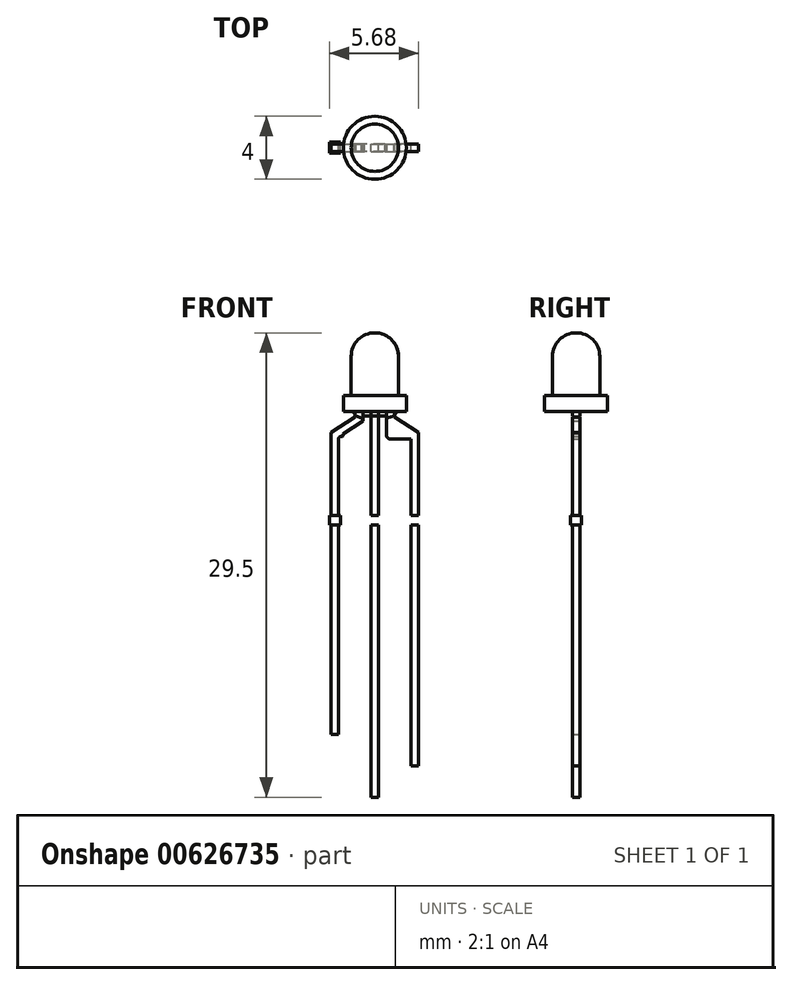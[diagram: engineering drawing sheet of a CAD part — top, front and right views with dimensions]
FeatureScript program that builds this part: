
annotation { "Feature Type Name" : "Feature", "Feature Type Description" : "" }
export const myFeature = defineFeature(function(context is Context, id is Id, definition is map)
    precondition{}
    {
        {
            var Q0;
            Q0=qCreatedBy(makeId("Front.planeOp"),FACE);
            var sketch = newSketch(context, id + "F0", { "sketchPlane" : qUnion([Q0])});
            skLineSegment(sketch, "E0", {"start": v(0, 0) * mm, "end": v(2, 0) * mm});
            skLineSegment(sketch, "E1", {"start": v(2, 0) * mm, "end": v(2, 1) * mm});
            skLineSegment(sketch, "E2", {"start": v(0, 0) * mm, "end": v(0, 1) * mm});
            skLineSegment(sketch, "E3", {"start": v(0, 1) * mm, "end": v(1.5, 1) * mm});
            skLineSegment(sketch, "E4", {"start": v(1.5, 1) * mm, "end": v(1.5, 3.5) * mm});
            skLineSegment(sketch, "E5", {"start": v(0, 5) * mm, "end": v(0, 5) * mm});
            skArc(sketch, "E6.filletArc", {"start": v(1.5, 3.5) * mm, "mid": v(1.06, 4.56) * mm, "end": v(0, 5) * mm});
            skLineSegment(sketch, "E7", {"start": v(1.5, 1) * mm, "end": v(2, 1) * mm});
            skLineSegment(sketch, "E8", {"start": v(0, 5) * mm, "end": v(0, 1) * mm});
            skSolve(sketch);
        }
        {
            var Q0;
            Q0=makeQuery(id+"F0.imprint","IMPRINT",FACE,{"disambiguationData":[TD([[makeQuery(id+"F0.imprint","IMPRINT",EDGE,{"derivedFrom":sQuery(id+"F0.wireOp",EDGE,"E3")}),1.0]])]});
            var Q1;
            Q1=makeQuery(id+"F0.imprint","IMPRINT",FACE,{"disambiguationData":[TD([[makeQuery(id+"F0.imprint","IMPRINT",EDGE,{"derivedFrom":sQuery(id+"F0.wireOp",EDGE,"E0")}),1.0]])]});
            var Q2;
            Q2=sQuery(id+"F0.wireOp",EDGE,"E8");
            revolve(context, id + "F1", {"entities" : qUnion([Q0, Q1]), "axis" : qUnion([Q2]), "revolveType" : RevolveType.FULL});
        }
        {
            var Q0;
            Q0=qCreatedBy(makeId("Front.planeOp"),FACE);
            var sketch = newSketch(context, id + "F2", { "sketchPlane" : qUnion([Q0])});
            skLineSegment(sketch, "E9", {"start": v(0, 0) * mm, "end": v(0.25, 0) * mm});
            skLineSegment(sketch, "E10", {"start": v(0.25, 0) * mm, "end": v(0.25, -24.5) * mm});
            skLineSegment(sketch, "E11", {"start": v(0.25, -24.5) * mm, "end": v(-0.25, -24.5) * mm});
            skLineSegment(sketch, "E12", {"start": v(-0.25, -24.5) * mm, "end": v(-0.25, 0) * mm});
            skLineSegment(sketch, "E13", {"start": v(-0.25, 0) * mm, "end": v(0, 0) * mm});
            skLineSegment(sketch, "E14", {"start": v(-2.29, -20.5) * mm, "end": v(-2.8, -20.5) * mm});
            skLineSegment(sketch, "E15", {"start": v(-2.8, -20.5) * mm, "end": v(-2.8, -1.6) * mm});
            skLineSegment(sketch, "E16", {"start": v(-2.29, -20.5) * mm, "end": v(-2.29, -1.7) * mm});
            skLineSegment(sketch, "E17", {"start": v(2.3, -22.5) * mm, "end": v(2.8, -22.5) * mm});
            skLineSegment(sketch, "E18", {"start": v(2.3, -22.5) * mm, "end": v(2.3, -1.74) * mm});
            skLineSegment(sketch, "E19", {"start": v(2.8, -22.5) * mm, "end": v(2.8, -1.6) * mm});
            skLineSegment(sketch, "E20", {"start": v(-0.25, 0) * mm, "end": v(-0.75, 0) * mm});
            skLineSegment(sketch, "E21", {"start": v(-0.75, 0) * mm, "end": v(-0.75, -0.6) * mm});
            skLineSegment(sketch, "E22", {"start": v(-0.75, 0) * mm, "end": v(-1.25, 0) * mm});
            skLineSegment(sketch, "E23", {"start": v(0.25, 0) * mm, "end": v(0.75, 0) * mm});
            skLineSegment(sketch, "E24", {"start": v(0.75, 0) * mm, "end": v(0.75, -0.6) * mm});
            skLineSegment(sketch, "E25", {"start": v(0.75, 0) * mm, "end": v(1.25, 0) * mm});
            skLineSegment(sketch, "E26", {"start": v(-2.8, -1.6) * mm, "end": v(-2.8, -1.34) * mm});
            skLineSegment(sketch, "E27", {"start": v(-2.8, -1.34) * mm, "end": v(-1.25, -0.34) * mm});
            skLineSegment(sketch, "E28", {"start": v(-1.25, -0.34) * mm, "end": v(-1.25, 0) * mm});
            skLineSegment(sketch, "E29", {"start": v(2.8, -1.6) * mm, "end": v(2.8, -1.34) * mm});
            skLineSegment(sketch, "E30", {"start": v(2.8, -1.34) * mm, "end": v(1.25, -0.34) * mm});
            skLineSegment(sketch, "E31", {"start": v(1.25, -0.34) * mm, "end": v(1.25, 0) * mm});
            skLineSegment(sketch, "E32", {"start": v(0.75, -0.6) * mm, "end": v(0.75, -1.54) * mm});
            skLineSegment(sketch, "E33", {"start": v(0.95, -1.74) * mm, "end": v(2.3, -1.74) * mm});
            skPoint(sketch, "E34.visualSharp", {"position": v(0.75, -1.74) * mm});
            skArc(sketch, "E34.filletArc", {"start": v(0.75, -1.54) * mm, "mid": v(0.8, -1.68) * mm, "end": v(0.95, -1.74) * mm});
            skLineSegment(sketch, "E35", {"start": v(-2.19, -1.6) * mm, "end": v(-2.1, -1.6) * mm});
            skLineSegment(sketch, "E36", {"start": v(-2, -1.5) * mm, "end": v(-2, -1.41) * mm});
            skLineSegment(sketch, "E37", {"start": v(-0.75, -0.6) * mm, "end": v(-2, -1.41) * mm});
            skPoint(sketch, "E38.visualSharp", {"position": v(-2.29, -1.6) * mm});
            skArc(sketch, "E38.filletArc", {"start": v(-2.19, -1.6) * mm, "mid": v(-2.26, -1.63) * mm, "end": v(-2.29, -1.7) * mm});
            skPoint(sketch, "E39.visualSharp", {"position": v(-2, -1.6) * mm});
            skArc(sketch, "E39.filletArc", {"start": v(-2.1, -1.6) * mm, "mid": v(-2.03, -1.57) * mm, "end": v(-2, -1.5) * mm});
            skLineSegment(sketch, "E40", {"start": v(0, -6.6) * mm, "end": v(4.77, -6.6) * mm});
            skLineSegment(sketch, "E41", {"start": v(0, -6.6) * mm, "end": v(-4.5, -6.6) * mm});
            skLineSegment(sketch, "E42", {"start": v(-2.8, -6.6) * mm, "end": v(-2.89, -6.6) * mm});
            skLineSegment(sketch, "E43", {"start": v(-2.89, -6.6) * mm, "end": v(-2.89, -7.2) * mm});
            skLineSegment(sketch, "E44", {"start": v(-2.89, -7.2) * mm, "end": v(-2.8, -7.2) * mm});
            skLineSegment(sketch, "E45", {"start": v(-2.29, -6.6) * mm, "end": v(-2.2, -6.6) * mm});
            skLineSegment(sketch, "E46", {"start": v(-2.2, -6.6) * mm, "end": v(-2.2, -7.2) * mm});
            skLineSegment(sketch, "E47", {"start": v(-2.2, -7.2) * mm, "end": v(-2.29, -7.2) * mm});
            skLineSegment(sketch, "E48.bottom", {"start": v(-0.25, -6.6) * mm, "end": v(-0.35, -6.6) * mm});
            skLineSegment(sketch, "E48.top", {"start": v(-0.25, -7.2) * mm, "end": v(-0.35, -7.2) * mm});
            skLineSegment(sketch, "E48.left", {"start": v(-0.25, -6.6) * mm, "end": v(-0.25, -7.2) * mm});
            skLineSegment(sketch, "E48.right", {"start": v(-0.35, -6.6) * mm, "end": v(-0.35, -7.2) * mm});
            skLineSegment(sketch, "E49.bottom", {"start": v(0.25, -6.6) * mm, "end": v(0.35, -6.6) * mm});
            skLineSegment(sketch, "E49.top", {"start": v(0.25, -7.2) * mm, "end": v(0.35, -7.2) * mm});
            skLineSegment(sketch, "E49.left", {"start": v(0.25, -6.6) * mm, "end": v(0.25, -7.2) * mm});
            skLineSegment(sketch, "E49.right", {"start": v(0.35, -6.6) * mm, "end": v(0.35, -7.2) * mm});
            skLineSegment(sketch, "E50.bottom", {"start": v(2.3, -6.6) * mm, "end": v(2.2, -6.6) * mm});
            skLineSegment(sketch, "E50.top", {"start": v(2.3, -7.2) * mm, "end": v(2.2, -7.2) * mm});
            skLineSegment(sketch, "E50.left", {"start": v(2.3, -6.6) * mm, "end": v(2.3, -7.2) * mm});
            skLineSegment(sketch, "E50.right", {"start": v(2.2, -6.6) * mm, "end": v(2.2, -7.2) * mm});
            skLineSegment(sketch, "E51.bottom", {"start": v(2.8, -6.6) * mm, "end": v(2.9, -6.6) * mm});
            skLineSegment(sketch, "E51.top", {"start": v(2.8, -7.2) * mm, "end": v(2.9, -7.2) * mm});
            skLineSegment(sketch, "E51.left", {"start": v(2.8, -6.6) * mm, "end": v(2.8, -7.2) * mm});
            skLineSegment(sketch, "E51.right", {"start": v(2.9, -6.6) * mm, "end": v(2.9, -7.2) * mm});
            skLineSegment(sketch, "E52.bottom", {"start": v(-2.89, -6.6) * mm, "end": v(-2.2, -6.6) * mm});
            skLineSegment(sketch, "E52.top", {"start": v(-2.89, -7.2) * mm, "end": v(-2.2, -7.2) * mm});
            skLineSegment(sketch, "E53.bottom", {"start": v(-0.35, -6.6) * mm, "end": v(0.35, -6.6) * mm});
            skLineSegment(sketch, "E53.top", {"start": v(-0.35, -7.2) * mm, "end": v(0.35, -7.2) * mm});
            skLineSegment(sketch, "E54.bottom", {"start": v(2.2, -6.6) * mm, "end": v(2.9, -6.6) * mm});
            skLineSegment(sketch, "E54.top", {"start": v(2.2, -7.2) * mm, "end": v(2.9, -7.2) * mm});
            skSolve(sketch);
        }
        {
            var Q0;
            Q0=makeQuery(id+"F2.imprint","IMPRINT",FACE,{"disambiguationData":[TD([[makeQuery(id+"F2.imprint","IMPRINT",EDGE,{"derivedFrom":sQuery(id+"F2.wireOp",EDGE,"E14")}),-1.0]])]});
            var Q1;
            Q1=makeQuery(id+"F2.imprint","IMPRINT",FACE,{"disambiguationData":[TD([[makeQuery(id+"F2.imprint","IMPRINT",EDGE,{"derivedFrom":sQuery(id+"F2.wireOp",EDGE,"E9")}),-1.0]])]});
            var Q2;
            Q2=makeQuery(id+"F2.imprint","IMPRINT",FACE,{"disambiguationData":[TD([[makeQuery(id+"F2.imprint","IMPRINT",EDGE,{"derivedFrom":sQuery(id+"F2.wireOp",EDGE,"E17")}),1.0]])]});
            var Q3;
            Q3=makeQuery(id+"F2.imprint","IMPRINT",FACE,{"disambiguationData":[TD([[makeQuery(id+"F2.imprint","IMPRINT",EDGE,{"derivedFrom":sQuery(id+"F2.wireOp",EDGE,"E24")}),1.0]])]});
            var Q4;
            Q4=makeQuery(id+"F2.imprint","IMPRINT",FACE,{"disambiguationData":[TD([[makeQuery(id+"F2.imprint","IMPRINT",EDGE,{"derivedFrom":sQuery(id+"F2.wireOp",EDGE,"E21")}),-1.0]])]});
            var Q5;
            {var subQ0=sQuery(id+"F2.wireOp",EDGE,"E11");Q5=makeQuery(id+"F2.imprint","IMPRINT",FACE,{"disambiguationData":[TD([[makeQuery(id+"F2.imprint","IMPRINT",EDGE,{"derivedFrom":subQ0}),-1.0]])]});}
            extrude(context, id + "F3", {"entities" : qUnion([Q0, Q1, Q2, Q3, Q4, Q5]), "endBound" : BoundingType.SYMMETRIC, "depth" : 0.5 * mm, "offsetDistance" : 25 * mm});
        }
        {
            var Q0;
            Q0=qCreatedBy(makeId("Front.planeOp"),FACE);
            var sketch = newSketch(context, id + "F4", { "sketchPlane" : qUnion([Q0])});
            skLineSegment(sketch, "E55", {"start": v(0, 0) * mm, "end": v(0, -0.3) * mm});
            skLineSegment(sketch, "E56", {"start": v(0, -0.3) * mm, "end": v(0.42, -0.3) * mm});
            skLineSegment(sketch, "E57", {"start": v(0, -0.3) * mm, "end": v(-0.42, -0.3) * mm});
            skLineSegment(sketch, "E58", {"start": v(0.42, -0.3) * mm, "end": v(0.65, -0.3) * mm});
            skLineSegment(sketch, "E59", {"start": v(0.65, -0.3) * mm, "end": v(0.76, -0.4) * mm});
            skLineSegment(sketch, "E60", {"start": v(0.76, -0.4) * mm, "end": v(1.21, -0.27) * mm});
            skLineSegment(sketch, "E61", {"start": v(1.21, -0.27) * mm, "end": v(1.4, 0) * mm});
            skLineSegment(sketch, "E62", {"start": v(-0.42, -0.3) * mm, "end": v(-0.65, -0.3) * mm});
            skLineSegment(sketch, "E63", {"start": v(-0.65, -0.3) * mm, "end": v(-0.83, -0.4) * mm});
            skLineSegment(sketch, "E64", {"start": v(-0.83, -0.4) * mm, "end": v(-1.2, -0.27) * mm});
            skLineSegment(sketch, "E65", {"start": v(-1.2, -0.27) * mm, "end": v(-1.4, 0) * mm});
            skLineSegment(sketch, "E66", {"start": v(-1.4, 0) * mm, "end": v(1.4, 0) * mm});
            skSolve(sketch);
        }
        {
            var Q0;
            {var subQ0=sQuery(id+"F4.wireOp",EDGE,"E55");Q0=makeQuery(id+"F4.imprint","IMPRINT",FACE,{"disambiguationData":[TD([[makeQuery(id+"F4.imprint","IMPRINT",EDGE,{"derivedFrom":subQ0}),-1.0]])]});}
            var Q1;
            {var subQ1=sQuery(id+"F4.wireOp",EDGE,"E55");Q1=makeQuery(id+"F4.imprint","IMPRINT",FACE,{"disambiguationData":[TD([[makeQuery(id+"F4.imprint","IMPRINT",EDGE,{"derivedFrom":subQ1}),1.0]])]});}
            extrude(context, id + "F5", {"entities" : qUnion([Q0, Q1]), "endBound" : BoundingType.SYMMETRIC, "depth" : 0.5 * mm, "offsetDistance" : 25 * mm});
        }
        {
            var Q0;
            {var subQ0=sQuery(id+"F2.wireOp",EDGE,"E52.top");var subQ1=sQuery(id+"F2.wireOp",EDGE,"E15");var subQ2=makeQuery(id+"F2.imprint","INTERSECT",VERTEX,{"derivedFrom":[subQ1,subQ0]});Q0=makeQuery(id+"F2.imprint","IMPRINT",FACE,{"disambiguationData":[TD([[makeQuery(id+"F2.imprint","IMPRINT",EDGE,{"disambiguationData":[TD([[subQ2,-1.0]])],"derivedFrom":subQ1}),-1.0]])]});}
            var Q1;
            {var subQ5=sQuery(id+"F2.wireOp",EDGE,"E43");Q1=makeQuery(id+"F2.imprint","IMPRINT",FACE,{"disambiguationData":[TD([[makeQuery(id+"F2.imprint","IMPRINT",EDGE,{"derivedFrom":subQ5}),1.0]])]});}
            var Q2;
            {var subQ5=sQuery(id+"F2.wireOp",EDGE,"E46");Q2=makeQuery(id+"F2.imprint","IMPRINT",FACE,{"disambiguationData":[TD([[makeQuery(id+"F2.imprint","IMPRINT",EDGE,{"derivedFrom":subQ5}),-1.0]])]});}
            var Q3;
            {var subQ0=sQuery(id+"F2.wireOp",EDGE,"E48.left");Q3=makeQuery(id+"F2.imprint","IMPRINT",FACE,{"disambiguationData":[TD([[makeQuery(id+"F2.imprint","IMPRINT",EDGE,{"derivedFrom":subQ0}),1.0]])]});}
            var Q4;
            {var subQ0=sQuery(id+"F2.wireOp",EDGE,"E48.left");Q4=makeQuery(id+"F2.imprint","IMPRINT",FACE,{"disambiguationData":[TD([[makeQuery(id+"F2.imprint","IMPRINT",EDGE,{"derivedFrom":subQ0}),-1.0]])]});}
            var Q5;
            {var subQ0=sQuery(id+"F2.wireOp",EDGE,"E50.left");Q5=makeQuery(id+"F2.imprint","IMPRINT",FACE,{"disambiguationData":[TD([[makeQuery(id+"F2.imprint","IMPRINT",EDGE,{"derivedFrom":subQ0}),1.0]])]});}
            var Q6;
            {var subQ0=sQuery(id+"F2.wireOp",EDGE,"E50.left");Q6=makeQuery(id+"F2.imprint","IMPRINT",FACE,{"disambiguationData":[TD([[makeQuery(id+"F2.imprint","IMPRINT",EDGE,{"derivedFrom":subQ0}),-1.0]])]});}
            var Q7;
            {var subQ0=sQuery(id+"F2.wireOp",EDGE,"E51.left");Q7=makeQuery(id+"F2.imprint","IMPRINT",FACE,{"disambiguationData":[TD([[makeQuery(id+"F2.imprint","IMPRINT",EDGE,{"derivedFrom":subQ0}),1.0]])]});}
            extrude(context, id + "F6", {"entities" : qUnion([Q0, Q1, Q2, Q3, Q4, Q5, Q6, Q7]), "endBound" : BoundingType.SYMMETRIC, "depth" : 0.7 * mm, "offsetDistance" : 25 * mm});
        }
    });
